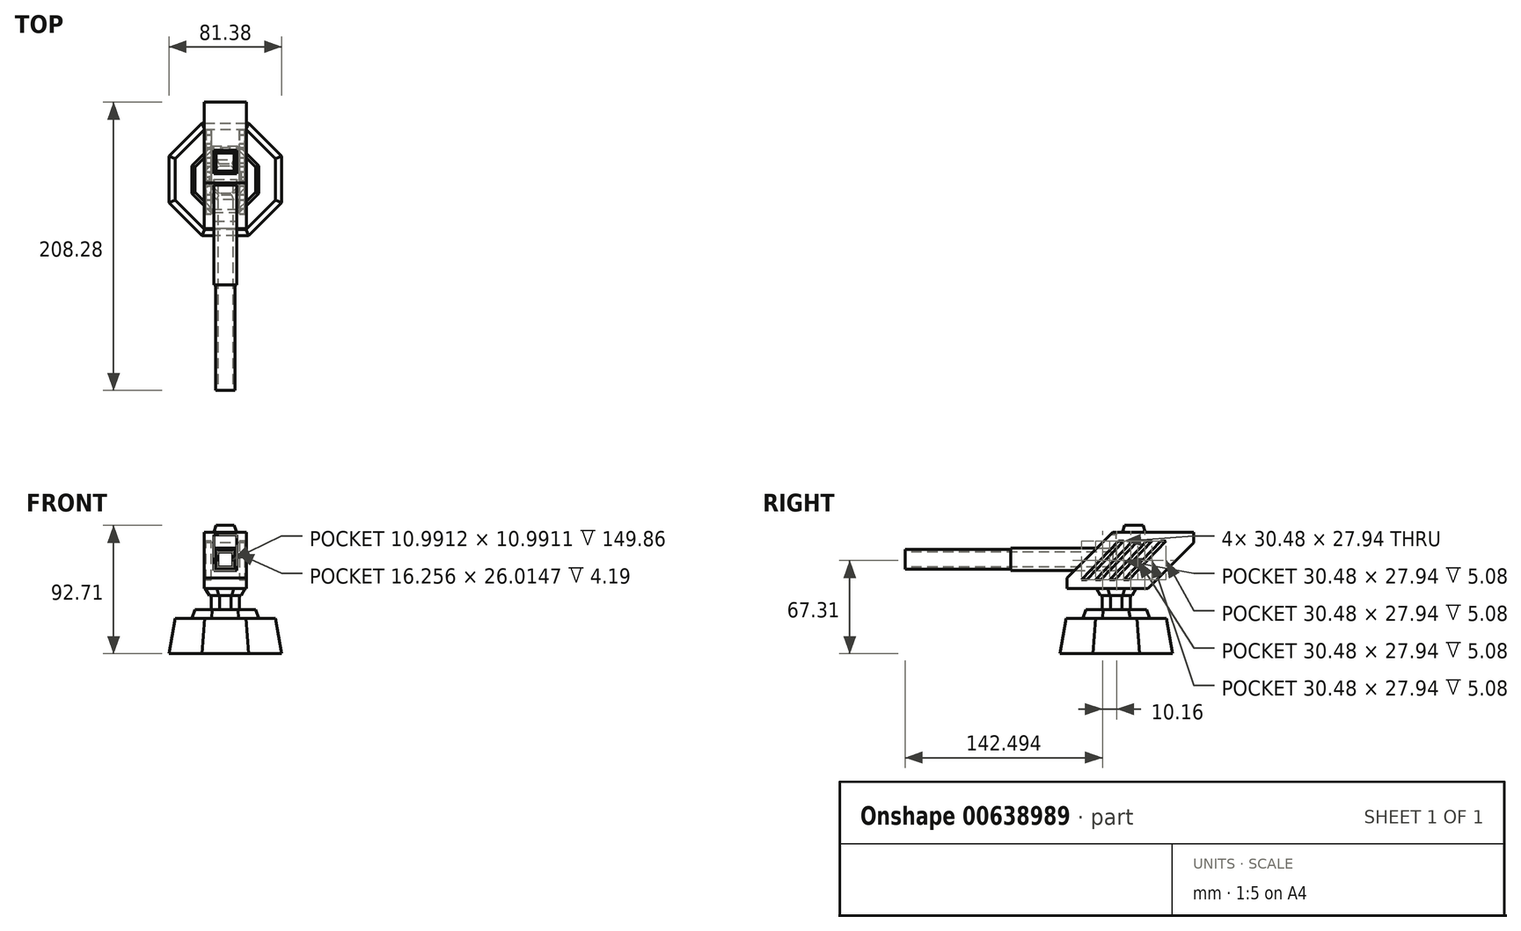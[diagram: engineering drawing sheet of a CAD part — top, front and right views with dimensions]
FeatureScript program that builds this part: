
annotation { "Feature Type Name" : "Feature", "Feature Type Description" : "" }
export const myFeature = defineFeature(function(context is Context, id is Id, definition is map)
    precondition{}
    {
        {
            var Q0;
            Q0=qCreatedBy(makeId("Top.planeOp"),FACE);
            var sketch = newSketch(context, id + "F0", { "sketchPlane" : qUnion([Q0])});
            skLineSegment(sketch, "E0", {"start": v(0, 0) * mm, "end": v(40.69, 16.85) * mm});
            skLineSegment(sketch, "E1", {"start": v(0, 0) * mm, "end": v(0, 37.13) * mm});
            skCircle(sketch, "E2.cCircle", {"center": v(0, 0) * mm, "radius": 44.04 * mm, "construction": true});
            skLineSegment(sketch, "E2.0", {"start": v(40.69, 16.85) * mm, "end": v(40.69, -16.85) * mm});
            skLineSegment(sketch, "E2.1", {"start": v(40.69, -16.85) * mm, "end": v(16.85, -40.69) * mm});
            skLineSegment(sketch, "E2.2", {"start": v(16.85, -40.69) * mm, "end": v(-16.85, -40.69) * mm});
            skLineSegment(sketch, "E2.3", {"start": v(-16.85, -40.69) * mm, "end": v(-40.69, -16.85) * mm});
            skLineSegment(sketch, "E2.4", {"start": v(-40.69, -16.85) * mm, "end": v(-40.69, 16.85) * mm});
            skLineSegment(sketch, "E2.5", {"start": v(-40.69, 16.85) * mm, "end": v(-16.85, 40.69) * mm});
            skLineSegment(sketch, "E2.6", {"start": v(-16.85, 40.69) * mm, "end": v(16.85, 40.69) * mm});
            skLineSegment(sketch, "E2.7", {"start": v(16.85, 40.69) * mm, "end": v(40.69, 16.85) * mm});
            skLineSegment(sketch, "E3", {"start": v(0, 40.69) * mm, "end": v(0, 37.13) * mm});
            skSolve(sketch);
        }
        {
            var Q0;
            Q0=qSketchRegion(id+"F0",true);
            extrude(context, id + "F1", {"entities" : qUnion([Q0]), "depth" : 25.4 * mm, "hasDraft" : true, "draftAngle" : 10 * degree, "draftPullDirection" : true});
        }
        {
            var Q0;
            Q0=makeQuery(id+"F1.opExtrude","CAP_FACE",FACE,{"disambiguationData":[OSD([sQuery(id+"F0.wireOp",EDGE,"E2.0"),sQuery(id+"F0.wireOp",EDGE,"E2.1"),sQuery(id+"F0.wireOp",EDGE,"E2.2"),sQuery(id+"F0.wireOp",EDGE,"E2.3"),sQuery(id+"F0.wireOp",EDGE,"E2.4"),sQuery(id+"F0.wireOp",EDGE,"E2.5"),sQuery(id+"F0.wireOp",EDGE,"E2.6"),sQuery(id+"F0.wireOp",EDGE,"E2.7")])],"isStart":false});
            var sketch = newSketch(context, id + "F2", { "sketchPlane" : qUnion([Q0])});
            skLineSegment(sketch, "E4", {"start": v(-15, 36.2) * mm, "end": v(-10.01, 24.17) * mm});
            skCircle(sketch, "E5.cCircle", {"center": v(0, 0) * mm, "radius": 26.16 * mm, "construction": true});
            skLineSegment(sketch, "E5.0", {"start": v(-10.01, 24.17) * mm, "end": v(10.01, 24.17) * mm});
            skLineSegment(sketch, "E5.1", {"start": v(10.01, 24.17) * mm, "end": v(24.17, 10.01) * mm});
            skLineSegment(sketch, "E5.2", {"start": v(24.17, 10.01) * mm, "end": v(24.17, -10.01) * mm});
            skLineSegment(sketch, "E5.3", {"start": v(24.17, -10.01) * mm, "end": v(10.01, -24.17) * mm});
            skLineSegment(sketch, "E5.4", {"start": v(10.01, -24.17) * mm, "end": v(-10.01, -24.17) * mm});
            skLineSegment(sketch, "E5.5", {"start": v(-10.01, -24.17) * mm, "end": v(-24.17, -10.01) * mm});
            skLineSegment(sketch, "E5.6", {"start": v(-24.17, -10.01) * mm, "end": v(-24.17, 10.01) * mm});
            skLineSegment(sketch, "E5.7", {"start": v(-24.17, 10.01) * mm, "end": v(-10.01, 24.17) * mm});
            skSolve(sketch);
        }
        {
            var Q0;
            Q0=makeQuery(id+"F2.imprint","IMPRINT",FACE,{"disambiguationData":[TD([[makeQuery(id+"F2.imprint","IMPRINT",EDGE,{"derivedFrom":sQuery(id+"F2.wireOp",EDGE,"E5.0")}),-1.0]])]});
            extrude(context, id + "F3", {"entities" : qUnion([Q0]), "depth" : 6.35 * mm, "hasDraft" : true, "draftAngle" : 20 * degree, "draftPullDirection" : true});
        }
        {
            var Q0;
            Q0=makeQuery(id+"F3.opExtrude","CAP_FACE",FACE,{"disambiguationData":[OSD([sQuery(id+"F2.wireOp",EDGE,"E5.0"),sQuery(id+"F2.wireOp",EDGE,"E5.1"),sQuery(id+"F2.wireOp",EDGE,"E5.2"),sQuery(id+"F2.wireOp",EDGE,"E5.3"),sQuery(id+"F2.wireOp",EDGE,"E5.4"),sQuery(id+"F2.wireOp",EDGE,"E5.5"),sQuery(id+"F2.wireOp",EDGE,"E5.6"),sQuery(id+"F2.wireOp",EDGE,"E5.7")])],"isStart":false});
            var sketch = newSketch(context, id + "F4", { "sketchPlane" : qUnion([Q0])});
            skLineSegment(sketch, "E6", {"start": v(-21.86, 0) * mm, "end": v(-14.37, 0) * mm});
            skPoint(sketch, "E6.endSnap0", {"position": v(-21.86, 0) * mm});
            skLineSegment(sketch, "E7", {"start": v(-9.06, 21.86) * mm, "end": v(-4.16, 10.04) * mm});
            skCircle(sketch, "E8.cCircle", {"center": v(0, 0) * mm, "radius": 10.87 * mm, "construction": true});
            skLineSegment(sketch, "E8.0", {"start": v(-4.16, 10.04) * mm, "end": v(4.16, 10.04) * mm});
            skLineSegment(sketch, "E8.1", {"start": v(4.16, 10.04) * mm, "end": v(10.04, 4.16) * mm});
            skLineSegment(sketch, "E8.2", {"start": v(10.04, 4.16) * mm, "end": v(10.04, -4.16) * mm});
            skLineSegment(sketch, "E8.3", {"start": v(10.04, -4.16) * mm, "end": v(4.16, -10.04) * mm});
            skLineSegment(sketch, "E8.4", {"start": v(4.16, -10.04) * mm, "end": v(-4.16, -10.04) * mm});
            skLineSegment(sketch, "E8.5", {"start": v(-4.16, -10.04) * mm, "end": v(-10.04, -4.16) * mm});
            skLineSegment(sketch, "E8.6", {"start": v(-10.04, -4.16) * mm, "end": v(-10.04, 4.16) * mm});
            skLineSegment(sketch, "E8.7", {"start": v(-10.04, 4.16) * mm, "end": v(-4.16, 10.04) * mm});
            skSolve(sketch);
        }
        {
            var Q0;
            Q0=qSketchRegion(id+"F4",true);
            extrude(context, id + "F5", {"entities" : qUnion([Q0]), "depth" : 10.16 * mm});
        }
        {
            var Q0;
            Q0=makeQuery(id+"F5.opExtrude","CAP_FACE",FACE,{"disambiguationData":[OSD([sQuery(id+"F4.wireOp",EDGE,"E8.0"),sQuery(id+"F4.wireOp",EDGE,"E8.1"),sQuery(id+"F4.wireOp",EDGE,"E8.2"),sQuery(id+"F4.wireOp",EDGE,"E8.3"),sQuery(id+"F4.wireOp",EDGE,"E8.4"),sQuery(id+"F4.wireOp",EDGE,"E8.5"),sQuery(id+"F4.wireOp",EDGE,"E8.6"),sQuery(id+"F4.wireOp",EDGE,"E8.7")])],"isStart":false});
            var sketch = newSketch(context, id + "F6", { "sketchPlane" : qUnion([Q0])});
            skLineSegment(sketch, "E9", {"start": v(-4.16, 10.04) * mm, "end": v(-4.76, 11.5) * mm});
            skCircle(sketch, "E10.cCircle", {"center": v(0, 0) * mm, "radius": 12.44 * mm, "construction": true});
            skLineSegment(sketch, "E10.0", {"start": v(-4.76, 11.5) * mm, "end": v(4.76, 11.5) * mm});
            skLineSegment(sketch, "E10.1", {"start": v(4.76, 11.5) * mm, "end": v(11.5, 4.76) * mm});
            skLineSegment(sketch, "E10.2", {"start": v(11.5, 4.76) * mm, "end": v(11.5, -4.76) * mm});
            skLineSegment(sketch, "E10.3", {"start": v(11.5, -4.76) * mm, "end": v(4.76, -11.5) * mm});
            skLineSegment(sketch, "E10.4", {"start": v(4.76, -11.5) * mm, "end": v(-4.76, -11.5) * mm});
            skLineSegment(sketch, "E10.5", {"start": v(-4.76, -11.5) * mm, "end": v(-11.5, -4.76) * mm});
            skLineSegment(sketch, "E10.6", {"start": v(-11.5, -4.76) * mm, "end": v(-11.5, 4.76) * mm});
            skLineSegment(sketch, "E10.7", {"start": v(-11.5, 4.76) * mm, "end": v(-4.76, 11.5) * mm});
            skSolve(sketch);
        }
        {
            var Q0;
            Q0=qSketchRegion(id+"F6",true);
            extrude(context, id + "F7", {"entities" : qUnion([Q0]), "depth" : 5.08 * mm, "hasDraft" : true, "draftAngle" : 30 * degree});
        }
        {
            var Q0;
            Q0=qCreatedBy(makeId("Right.planeOp"),FACE);
            var sketch = newSketch(context, id + "F8", { "sketchPlane" : qUnion([Q0])});
            skLineSegment(sketch, "E11.0", {"start": v(5.97, 47) * mm, "end": v(-5.97, 47) * mm});
            skLineSegment(sketch, "E12", {"start": v(-5.97, 47) * mm, "end": v(-35.56, 47) * mm});
            skLineSegment(sketch, "E13", {"start": v(-35.56, 47) * mm, "end": v(22.86, 47) * mm});
            skPoint(sketch, "E14", {"position": v(0, 47) * mm});
            skLineSegment(sketch, "E15", {"start": v(-35.56, 47) * mm, "end": v(-35.56, 87.63) * mm});
            skLineSegment(sketch, "E16", {"start": v(-2.54, 87.63) * mm, "end": v(56.7, 87.63) * mm});
            skLineSegment(sketch, "E17", {"start": v(55.88, 47) * mm, "end": v(55.88, 87.63) * mm});
            skPoint(sketch, "E18", {"position": v(55.88, 80.01) * mm});
            skLineSegment(sketch, "E19", {"start": v(55.88, 80.01) * mm, "end": v(22.86, 47) * mm});
            skPoint(sketch, "E20", {"position": v(-35.56, 54.61) * mm});
            skLineSegment(sketch, "E21", {"start": v(-35.56, 54.61) * mm, "end": v(-2.54, 87.63) * mm});
            skLineSegment(sketch, "E22", {"start": v(55.88, 87.63) * mm, "end": v(56.7, 87.63) * mm});
            skSolve(sketch);
        }
        {
            var Q0;
            Q0=qSketchRegion(id+"F8",true);
            extrude(context, id + "F9", {"entities" : qUnion([Q0]), "endBound" : BoundingType.SYMMETRIC, "depth" : 30.48 * mm});
        }
        {
            var Q0;
            Q0=makeQuery(id+"F9.opExtrude","SWEPT_FACE",FACE,{"disambiguationData":[OSD([sQuery(id+"F8.wireOp",EDGE,"E15")])]});
            var sketch = newSketch(context, id + "F10", { "sketchPlane" : qUnion([Q0])});
            skLineSegment(sketch, "E23.0", {"start": v(15.24, 54.61) * mm, "end": v(-15.24, 54.61) * mm});
            skPoint(sketch, "E24", {"position": v(-8.13, 54.61) * mm});
            skPoint(sketch, "E25", {"position": v(8.13, 54.61) * mm});
            skLineSegment(sketch, "E26", {"start": v(-8.13, 54.61) * mm, "end": v(-8.13, 85.98) * mm});
            skLineSegment(sketch, "E27", {"start": v(-8.13, 85.98) * mm, "end": v(10.84, 85.98) * mm});
            skLineSegment(sketch, "E28", {"start": v(8.13, 54.61) * mm, "end": v(8.13, 85.98) * mm});
            skLineSegment(sketch, "E29", {"start": v(-8.13, 59.97) * mm, "end": v(8.13, 59.97) * mm});
            skSolve(sketch);
        }
        {
            var Q0;
            {var subQ3=sQuery(id+"F10.wireOp",EDGE,"E29");Q0=makeQuery(id+"F10.imprint","IMPRINT",FACE,{"disambiguationData":[TD([[makeQuery(id+"F10.imprint","IMPRINT",EDGE,{"derivedFrom":subQ3}),1.0]])]});}
            extrude(context, id + "F11", {"entities" : qUnion([Q0]), "operationType" : NewBodyOperationType.REMOVE, "oppositeDirection" : true, "depth" : 35.56 * mm});
        }
        {
            var Q0;
            Q0=makeQuery(id+"F11.boolean.opBoolean","COPY",FACE,{"derivedFrom":makeQuery(id+"F11.opExtrude","CAP_FACE",FACE,{"disambiguationData":[OSD([sQuery(id+"F10.wireOp",EDGE,"E23.0"),sQuery(id+"F10.wireOp",EDGE,"E26"),sQuery(id+"F10.wireOp",EDGE,"E27"),sQuery(id+"F10.wireOp",EDGE,"E28")])],"isStart":false})});
            var sketch = newSketch(context, id + "F12", { "sketchPlane" : qUnion([Q0])});
            skLineSegment(sketch, "E30.0", {"start": v(-8.13, 76.22) * mm, "end": v(-8.13, 85.98) * mm});
            skLineSegment(sketch, "E31.0", {"start": v(8.13, 76.22) * mm, "end": v(8.13, 85.98) * mm});
            skLineSegment(sketch, "E32", {"start": v(-8.13, 76.22) * mm, "end": v(8.13, 76.22) * mm});
            skLineSegment(sketch, "E33.0", {"start": v(-8.13, 59.97) * mm, "end": v(-8.13, 85.98) * mm});
            skLineSegment(sketch, "E34.0", {"start": v(8.13, 59.97) * mm, "end": v(8.13, 85.98) * mm});
            skLineSegment(sketch, "E35", {"start": v(-8.13, 59.97) * mm, "end": v(8.13, 59.97) * mm});
            skSolve(sketch);
        }
        {
            var Q0;
            Q0=qSketchRegion(id+"F12",true);
            extrude(context, id + "F13", {"entities" : qUnion([Q0]), "depth" : 76.2 * mm});
        }
        {
            var Q0;
            Q0=makeQuery(id+"F13.opExtrude","CAP_FACE",FACE,{"disambiguationData":[OSD([sQuery(id+"F12.wireOp",EDGE,"E32"),sQuery(id+"F12.wireOp",EDGE,"E33.0"),sQuery(id+"F12.wireOp",EDGE,"E34.0"),sQuery(id+"F12.wireOp",EDGE,"E35")])],"isStart":false});
            var sketch = newSketch(context, id + "F14", { "sketchPlane" : qUnion([Q0])});
            skLineSegment(sketch, "E36.rect.bottom", {"start": v(-7.11, 75.2) * mm, "end": v(7.11, 75.2) * mm});
            skLineSegment(sketch, "E36.rect.top", {"start": v(-7.11, 60.98) * mm, "end": v(7.11, 60.98) * mm});
            skLineSegment(sketch, "E36.rect.left", {"start": v(-7.11, 75.2) * mm, "end": v(-7.11, 60.98) * mm});
            skLineSegment(sketch, "E36.rect.right", {"start": v(7.11, 75.2) * mm, "end": v(7.11, 60.98) * mm});
            skPoint(sketch, "E36.rect.middle", {"position": v(0, 68.1) * mm});
            skPoint(sketch, "E36.rect.middle.positionSnap0", {"position": v(-8.13, 68.1) * mm});
            skPoint(sketch, "E36.rect.middle.positionSnap1", {"position": v(0, 76.22) * mm});
            skPoint(sketch, "E36.rect.centerSnap0", {"position": v(-8.13, 68.1) * mm});
            skPoint(sketch, "E36.rect.centerSnap1", {"position": v(0, 76.22) * mm});
            skSolve(sketch);
        }
        {
            var Q0;
            Q0=qSketchRegion(id+"F14",true);
            extrude(context, id + "F15", {"entities" : qUnion([Q0]), "operationType" : NewBodyOperationType.ADD, "depth" : 76.2 * mm, "hasDraft" : true, "draftAngle" : 0 * degree, "draftPullDirection" : true});
        }
        {
            var Q0;
            Q0=makeQuery(id+"F15.opExtrude","CAP_FACE",FACE,{"disambiguationData":[OSD([sQuery(id+"F14.wireOp",EDGE,"E36.rect.bottom"),sQuery(id+"F14.wireOp",EDGE,"E36.rect.top"),sQuery(id+"F14.wireOp",EDGE,"E36.rect.left"),sQuery(id+"F14.wireOp",EDGE,"E36.rect.right")])],"isStart":false});
            var sketch = newSketch(context, id + "F16", { "sketchPlane" : qUnion([Q0])});
            skLineSegment(sketch, "E37", {"start": v(-7.11, 75.2) * mm, "end": v(-5.5, 73.59) * mm});
            skLineSegment(sketch, "E38.rect.bottom", {"start": v(-5.5, 73.59) * mm, "end": v(5.5, 73.59) * mm});
            skLineSegment(sketch, "E38.rect.top", {"start": v(-5.5, 62.6) * mm, "end": v(5.5, 62.6) * mm});
            skLineSegment(sketch, "E38.rect.left", {"start": v(-5.5, 73.59) * mm, "end": v(-5.5, 62.6) * mm});
            skLineSegment(sketch, "E38.rect.right", {"start": v(5.5, 73.59) * mm, "end": v(5.5, 62.6) * mm});
            skPoint(sketch, "E38.rect.middle", {"position": v(0, 68.1) * mm});
            skPoint(sketch, "E38.rect.middle.positionSnap0", {"position": v(-7.11, 68.1) * mm});
            skPoint(sketch, "E38.rect.middle.positionSnap1", {"position": v(0, 75.2) * mm});
            skPoint(sketch, "E38.rect.centerSnap0", {"position": v(-7.11, 68.1) * mm});
            skPoint(sketch, "E38.rect.centerSnap1", {"position": v(0, 75.2) * mm});
            skSolve(sketch);
        }
        {
            var Q0;
            Q0=qSketchRegion(id+"F16",true);
            extrude(context, id + "F17", {"entities" : qUnion([Q0]), "operationType" : NewBodyOperationType.REMOVE, "oppositeDirection" : true, "depth" : 149.86 * mm});
        }
        {
            var Q0;
            Q0=makeQuery(id+"F9.opExtrude","SWEPT_FACE",FACE,{"disambiguationData":[OSD([sQuery(id+"F8.wireOp",EDGE,"E16")])]});
            var sketch = newSketch(context, id + "F18", { "sketchPlane" : qUnion([Q0])});
            skLineSegment(sketch, "E39.rect.bottom", {"start": v(-8.38, 21.08) * mm, "end": v(8.38, 21.08) * mm});
            skLineSegment(sketch, "E39.rect.top", {"start": v(-8.38, 4.32) * mm, "end": v(8.38, 4.32) * mm});
            skLineSegment(sketch, "E39.rect.left", {"start": v(-8.38, 21.08) * mm, "end": v(-8.38, 4.32) * mm});
            skLineSegment(sketch, "E39.rect.right", {"start": v(8.38, 21.08) * mm, "end": v(8.38, 4.32) * mm});
            skPoint(sketch, "E39.rect.middle", {"position": v(0, 12.7) * mm});
            skSolve(sketch);
        }
        {
            var Q0;
            Q0=qSketchRegion(id+"F18",true);
            extrude(context, id + "F19", {"entities" : qUnion([Q0]), "depth" : 5.08 * mm, "hasDraft" : true, "draftAngle" : 20 * degree, "draftPullDirection" : true});
        }
        {
            var Q0;
            Q0=makeQuery(id+"F9.opExtrude","CAP_FACE",FACE,{"disambiguationData":[OSD([sQuery(id+"F8.wireOp",EDGE,"E13"),sQuery(id+"F8.wireOp",EDGE,"E15"),sQuery(id+"F8.wireOp",EDGE,"E16"),sQuery(id+"F8.wireOp",EDGE,"E17"),sQuery(id+"F8.wireOp",EDGE,"E19"),sQuery(id+"F8.wireOp",EDGE,"E21")])],"isStart":false});
            var sketch = newSketch(context, id + "F20", { "sketchPlane" : qUnion([Q0])});
            skPoint(sketch, "E40", {"position": v(-35.56, 53.34) * mm});
            skPoint(sketch, "E41", {"position": v(-8.89, 81.28) * mm});
            skPoint(sketch, "E42", {"position": v(1.52, 81.28) * mm});
            skPoint(sketch, "E43", {"position": v(5.33, 81.28) * mm});
            skPoint(sketch, "E44", {"position": v(11.68, 81.28) * mm});
            skPoint(sketch, "E45", {"position": v(15.5, 81.28) * mm});
            skPoint(sketch, "E46", {"position": v(21.84, 81.28) * mm});
            skPoint(sketch, "E47", {"position": v(25.65, 81.28) * mm});
            skPoint(sketch, "E48", {"position": v(-21.34, 53.34) * mm});
            skPoint(sketch, "E49", {"position": v(-25.15, 53.34) * mm});
            skPoint(sketch, "E50", {"position": v(-14.99, 53.34) * mm});
            skPoint(sketch, "E51", {"position": v(-11.18, 53.34) * mm});
            skPoint(sketch, "E52", {"position": v(-4.83, 53.34) * mm});
            skPoint(sketch, "E53", {"position": v(-1.02, 53.34) * mm});
            skLineSegment(sketch, "E54", {"start": v(1.52, 81.28) * mm, "end": v(-25.15, 53.34) * mm});
            skLineSegment(sketch, "E55", {"start": v(-21.34, 53.34) * mm, "end": v(-25.15, 53.34) * mm});
            skLineSegment(sketch, "E56", {"start": v(-21.34, 53.34) * mm, "end": v(5.33, 81.28) * mm});
            skLineSegment(sketch, "E57", {"start": v(5.33, 81.28) * mm, "end": v(1.52, 81.28) * mm});
            skLineSegment(sketch, "E58", {"start": v(11.68, 81.28) * mm, "end": v(-14.99, 53.34) * mm});
            skLineSegment(sketch, "E59", {"start": v(-11.18, 53.34) * mm, "end": v(-14.99, 53.34) * mm});
            skLineSegment(sketch, "E60", {"start": v(15.5, 81.28) * mm, "end": v(-11.18, 53.34) * mm});
            skLineSegment(sketch, "E61", {"start": v(11.68, 81.28) * mm, "end": v(15.5, 81.28) * mm});
            skLineSegment(sketch, "E62", {"start": v(21.84, 81.28) * mm, "end": v(-4.83, 53.34) * mm});
            skLineSegment(sketch, "E63", {"start": v(-1.02, 53.34) * mm, "end": v(25.65, 81.28) * mm});
            skPoint(sketch, "E64", {"position": v(32, 81.28) * mm});
            skPoint(sketch, "E65", {"position": v(35.81, 81.28) * mm});
            skPoint(sketch, "E66", {"position": v(5.33, 53.34) * mm});
            skPoint(sketch, "E67", {"position": v(9.14, 53.34) * mm});
            skLineSegment(sketch, "E68", {"start": v(5.33, 53.34) * mm, "end": v(32, 81.28) * mm});
            skLineSegment(sketch, "E69", {"start": v(32, 81.28) * mm, "end": v(35.81, 81.28) * mm});
            skLineSegment(sketch, "E70", {"start": v(35.81, 81.28) * mm, "end": v(9.14, 53.34) * mm});
            skLineSegment(sketch, "E71", {"start": v(9.14, 53.34) * mm, "end": v(5.33, 53.34) * mm});
            skLineSegment(sketch, "E72", {"start": v(-1.02, 53.34) * mm, "end": v(-4.83, 53.34) * mm});
            skLineSegment(sketch, "E73", {"start": v(21.84, 81.28) * mm, "end": v(25.65, 81.28) * mm});
            skSolve(sketch);
        }
        {
            var Q0;
            Q0=qSketchRegion(id+"F20",true);
            extrude(context, id + "F21", {"entities" : qUnion([Q0]), "operationType" : NewBodyOperationType.REMOVE, "oppositeDirection" : true, "depth" : 5.08 * mm});
        }
        {
            var Q0;
            Q0=makeQuery(id+"F9.opExtrude","CAP_FACE",FACE,{"disambiguationData":[OSD([sQuery(id+"F8.wireOp",EDGE,"E13"),sQuery(id+"F8.wireOp",EDGE,"E15"),sQuery(id+"F8.wireOp",EDGE,"E16"),sQuery(id+"F8.wireOp",EDGE,"E17"),sQuery(id+"F8.wireOp",EDGE,"E19"),sQuery(id+"F8.wireOp",EDGE,"E21")])],"isStart":true});
            var sketch = newSketch(context, id + "F22", { "sketchPlane" : qUnion([Q0])});
            skLineSegment(sketch, "E74.0.0", {"start": v(-5.33, 81.28) * mm, "end": v(-1.52, 81.28) * mm});
            skLineSegment(sketch, "E74.0.1", {"start": v(-1.52, 81.28) * mm, "end": v(25.15, 53.34) * mm});
            skLineSegment(sketch, "E74.0.2", {"start": v(25.15, 53.34) * mm, "end": v(21.34, 53.34) * mm});
            skLineSegment(sketch, "E74.0.3", {"start": v(21.34, 53.34) * mm, "end": v(-5.33, 81.28) * mm});
            skLineSegment(sketch, "E75.0.0", {"start": v(-15.5, 81.28) * mm, "end": v(-11.68, 81.28) * mm});
            skLineSegment(sketch, "E75.0.1", {"start": v(-11.68, 81.28) * mm, "end": v(14.99, 53.34) * mm});
            skLineSegment(sketch, "E75.0.2", {"start": v(14.99, 53.34) * mm, "end": v(11.18, 53.34) * mm});
            skLineSegment(sketch, "E75.0.3", {"start": v(11.18, 53.34) * mm, "end": v(-15.5, 81.28) * mm});
            skLineSegment(sketch, "E76.0.0", {"start": v(-25.65, 81.28) * mm, "end": v(-21.84, 81.28) * mm});
            skLineSegment(sketch, "E76.0.1", {"start": v(-21.84, 81.28) * mm, "end": v(4.83, 53.34) * mm});
            skLineSegment(sketch, "E76.0.2", {"start": v(4.83, 53.34) * mm, "end": v(1.02, 53.34) * mm});
            skLineSegment(sketch, "E76.0.3", {"start": v(1.02, 53.34) * mm, "end": v(-25.65, 81.28) * mm});
            skLineSegment(sketch, "E77.0.0", {"start": v(-32, 81.28) * mm, "end": v(-5.33, 53.34) * mm});
            skLineSegment(sketch, "E77.0.1", {"start": v(-5.33, 53.34) * mm, "end": v(-9.14, 53.34) * mm});
            skLineSegment(sketch, "E77.0.2", {"start": v(-9.14, 53.34) * mm, "end": v(-35.81, 81.28) * mm});
            skLineSegment(sketch, "E77.0.3", {"start": v(-35.81, 81.28) * mm, "end": v(-32, 81.28) * mm});
            skSolve(sketch);
        }
        {
            var Q0;
            Q0=qSketchRegion(id+"F22",true);
            extrude(context, id + "F23", {"entities" : qUnion([Q0]), "operationType" : NewBodyOperationType.REMOVE, "oppositeDirection" : true, "depth" : 5.08 * mm});
        }
        {
            var Q0;
            Q0=makeQuery(id+"F23.boolean.opBoolean","COPY",FACE,{"derivedFrom":makeQuery(id+"F23.opExtrude","CAP_FACE",FACE,{"disambiguationData":[OSD([sQuery(id+"F22.wireOp",EDGE,"E74.0.0"),sQuery(id+"F22.wireOp",EDGE,"E74.0.1"),sQuery(id+"F22.wireOp",EDGE,"E74.0.2"),sQuery(id+"F22.wireOp",EDGE,"E74.0.3")])],"isStart":false})});
            var sketch = newSketch(context, id + "F24", { "sketchPlane" : qUnion([Q0])});
            skLineSegment(sketch, "E78.0.0", {"start": v(-11.68, 81.28) * mm, "end": v(-15.5, 81.28) * mm});
            skLineSegment(sketch, "E78.0.1", {"start": v(-15.5, 81.28) * mm, "end": v(11.18, 53.34) * mm});
            skLineSegment(sketch, "E78.0.2", {"start": v(11.18, 53.34) * mm, "end": v(14.99, 53.34) * mm});
            skLineSegment(sketch, "E78.0.3", {"start": v(14.99, 53.34) * mm, "end": v(-11.68, 81.28) * mm});
            skLineSegment(sketch, "E79.0.0", {"start": v(-1.52, 81.28) * mm, "end": v(-5.33, 81.28) * mm});
            skLineSegment(sketch, "E79.0.1", {"start": v(-5.33, 81.28) * mm, "end": v(21.34, 53.34) * mm});
            skLineSegment(sketch, "E79.0.2", {"start": v(21.34, 53.34) * mm, "end": v(25.15, 53.34) * mm});
            skLineSegment(sketch, "E79.0.3", {"start": v(25.15, 53.34) * mm, "end": v(-1.52, 81.28) * mm});
            skLineSegment(sketch, "E80.0.0", {"start": v(-21.84, 81.28) * mm, "end": v(-25.65, 81.28) * mm});
            skLineSegment(sketch, "E80.0.1", {"start": v(-25.65, 81.28) * mm, "end": v(1.02, 53.34) * mm});
            skLineSegment(sketch, "E80.0.2", {"start": v(1.02, 53.34) * mm, "end": v(4.83, 53.34) * mm});
            skLineSegment(sketch, "E80.0.3", {"start": v(4.83, 53.34) * mm, "end": v(-21.84, 81.28) * mm});
            skLineSegment(sketch, "E81.0.0", {"start": v(-5.33, 53.34) * mm, "end": v(-32, 81.28) * mm});
            skLineSegment(sketch, "E81.0.1", {"start": v(-32, 81.28) * mm, "end": v(-35.81, 81.28) * mm});
            skLineSegment(sketch, "E81.0.2", {"start": v(-35.81, 81.28) * mm, "end": v(-9.14, 53.34) * mm});
            skLineSegment(sketch, "E81.0.3", {"start": v(-9.14, 53.34) * mm, "end": v(-5.33, 53.34) * mm});
            skSolve(sketch);
        }
        {
            var Q0;
            Q0=qSketchRegion(id+"F24",true);
            extrude(context, id + "F25", {"entities" : qUnion([Q0]), "depth" : 3.8 * mm});
        }
        {
            var Q0;
            Q0=makeQuery(id+"F21.boolean.opBoolean","COPY",FACE,{"derivedFrom":makeQuery(id+"F21.opExtrude","CAP_FACE",FACE,{"disambiguationData":[OSD([sQuery(id+"F20.wireOp",EDGE,"E58"),sQuery(id+"F20.wireOp",EDGE,"E59"),sQuery(id+"F20.wireOp",EDGE,"E60"),sQuery(id+"F20.wireOp",EDGE,"E61")])],"isStart":false})});
            var sketch = newSketch(context, id + "F26", { "sketchPlane" : qUnion([Q0])});
            skLineSegment(sketch, "E82.0.0", {"start": v(5.33, 81.28) * mm, "end": v(1.52, 81.28) * mm});
            skLineSegment(sketch, "E82.0.1", {"start": v(1.52, 81.28) * mm, "end": v(-25.15, 53.34) * mm});
            skLineSegment(sketch, "E82.0.2", {"start": v(-25.15, 53.34) * mm, "end": v(-21.34, 53.34) * mm});
            skLineSegment(sketch, "E82.0.3", {"start": v(-21.34, 53.34) * mm, "end": v(5.33, 81.28) * mm});
            skLineSegment(sketch, "E83.0.0", {"start": v(15.5, 81.28) * mm, "end": v(11.68, 81.28) * mm});
            skLineSegment(sketch, "E83.0.1", {"start": v(11.68, 81.28) * mm, "end": v(-14.99, 53.34) * mm});
            skLineSegment(sketch, "E83.0.2", {"start": v(-14.99, 53.34) * mm, "end": v(-11.18, 53.34) * mm});
            skLineSegment(sketch, "E83.0.3", {"start": v(-11.18, 53.34) * mm, "end": v(15.5, 81.28) * mm});
            skLineSegment(sketch, "E84.0.0", {"start": v(25.65, 81.28) * mm, "end": v(21.84, 81.28) * mm});
            skLineSegment(sketch, "E84.0.1", {"start": v(21.84, 81.28) * mm, "end": v(-4.83, 53.34) * mm});
            skLineSegment(sketch, "E84.0.2", {"start": v(-4.83, 53.34) * mm, "end": v(-1.02, 53.34) * mm});
            skLineSegment(sketch, "E84.0.3", {"start": v(-1.02, 53.34) * mm, "end": v(25.65, 81.28) * mm});
            skLineSegment(sketch, "E85.0.0", {"start": v(32, 81.28) * mm, "end": v(5.33, 53.34) * mm});
            skLineSegment(sketch, "E85.0.1", {"start": v(5.33, 53.34) * mm, "end": v(9.14, 53.34) * mm});
            skLineSegment(sketch, "E85.0.2", {"start": v(9.14, 53.34) * mm, "end": v(35.81, 81.28) * mm});
            skLineSegment(sketch, "E85.0.3", {"start": v(35.81, 81.28) * mm, "end": v(32, 81.28) * mm});
            skSolve(sketch);
        }
        {
            var Q0;
            Q0=qSketchRegion(id+"F26",true);
            extrude(context, id + "F27", {"entities" : qUnion([Q0]), "depth" : 3.8 * mm});
        }
    });
